# Revit family: Entro DV250
name_source: partatom
category: Mechanical Equipment
revit_build: Autodesk Revit MEP 2013 (Build: 20120221_2030)
units: mm (PartAtom-declared; Revit-internal decimal feet)

## types (1)
- DV250 Entro
    After Heater = Optional 400/700/1700 W
    Air Filters = 2 x G4 or 2 x F7 (optional)
    Air Volume m3/hr@ Pa = 230@100Pa
175@100Pa
    Anti frost protection = Included
    Carbon dioxide control (optional) = Yes
    Condensate pipe dia = 14 mm  [stored 0.0459318 ft]
    Control Optional = CO2,Humidity,Digital
    Control Standard = Manual Speed
    Depth mm = 280 mm  [stored 0.918635 ft]
    Duct Connections = 4 x 160mm dia
    EC motor for fine speed control and low SFP = Yes
    Electronic control panel with LCD display = Optional
    Filter maintenance reminder = Optional
    Frequency = 50Hz
    Heat Exchanger = Counterflow
    Heat Recovery = <95%
    Height mm = 660 mm
    Humidity control (optional) = Yes
    IP Rating = IP20
    Kitchen + 1 wet rooms = 0.70 W/l/s
    Kitchen + 2 wet rooms = 0.78 W/l/s
    Kitchen + 3 wet rooms = 0.93 W/l/s
    Kitchen + 4 wet rooms = 1.20 W/l/s
    Kitchen + 5 wet rooms = 1.38 W/l/s
    Max Air Volume  m3/hr = 280
    Meets Building Regulations Approved Document F 2010 = Yes
    Model = DV250 Entro
    Part Number = 90000397
    Passive House Certified = Yes
    Pre Heater = Optional 400/700/1700 W
    SAP Appendix Q Eligible = Yes
    Summer by-pass = Automatic 100%
    Summer/Winter by-pass = Yes
    Voltage Supply      Single Phase = 220-240v AC
    Warranty = 2 years
    Width mm = 850 mm  [stored 2.78871 ft]

note: [stored X ft] marks values corroborated as IEEE doubles in the binary element streams (Revit-internal decimal feet)

## geometry (parser evidence)
native form markers: Sweep x1
no freeform markers — native parametric forms only
